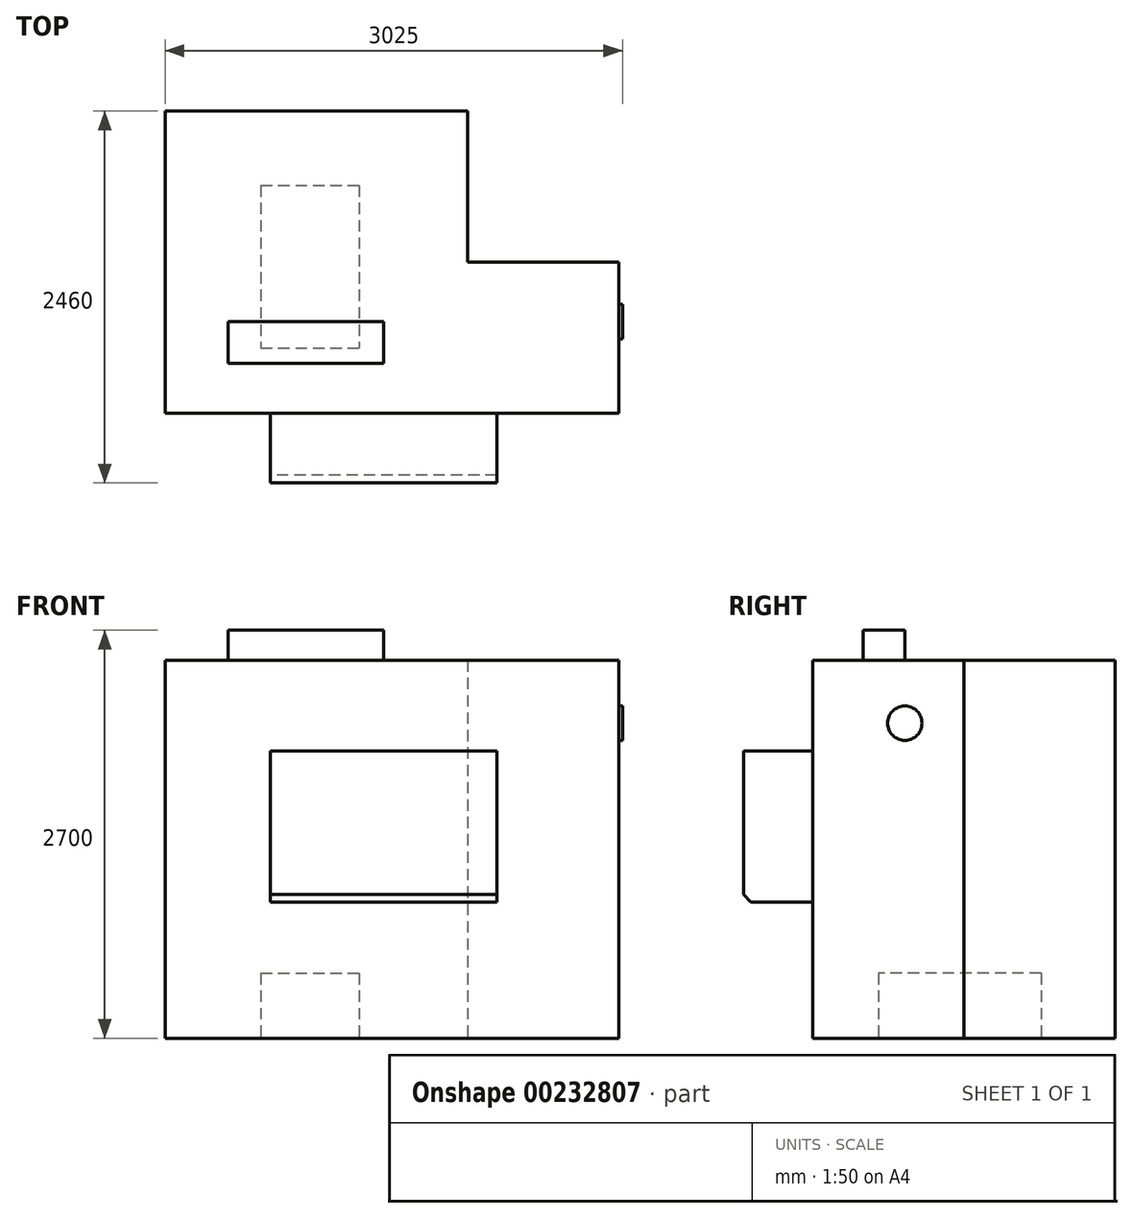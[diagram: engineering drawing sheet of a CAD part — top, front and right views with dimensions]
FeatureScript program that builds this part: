
annotation { "Feature Type Name" : "Feature", "Feature Type Description" : "" }
export const myFeature = defineFeature(function(context is Context, id is Id, definition is map)
    precondition{}
    {
        {
            var Q0;
            Q0=qCreatedBy(makeId("Top.planeOp"),FACE);
            var sketch = newSketch(context, id + "F0", { "sketchPlane" : qUnion([Q0])});
            skLineSegment(sketch, "E0", {"start": v(-1444.29, -607.78) * mm, "end": v(-1444.29, 1392.22) * mm});
            skLineSegment(sketch, "E1", {"start": v(-1444.29, 1392.22) * mm, "end": v(555.71, 1392.22) * mm});
            skLineSegment(sketch, "E2", {"start": v(555.71, 1392.22) * mm, "end": v(555.71, 392.22) * mm});
            skLineSegment(sketch, "E3", {"start": v(555.71, 392.22) * mm, "end": v(1555.71, 392.22) * mm});
            skLineSegment(sketch, "E4", {"start": v(1555.71, 392.22) * mm, "end": v(1555.71, -607.78) * mm});
            skLineSegment(sketch, "E5", {"start": v(1555.71, -607.78) * mm, "end": v(-1444.29, -607.78) * mm});
            skCircle(sketch, "E6", {"center": v(-627.12, 837.16) * mm, "radius": 250 * mm});
            skSolve(sketch);
        }
        {
            var Q0;
            Q0=makeQuery(id+"F0.imprint","IMPRINT",FACE,{"disambiguationData":[TD([[makeQuery(id+"F0.imprint","IMPRINT",EDGE,{"derivedFrom":sQuery(id+"F0.wireOp",EDGE,"E0")}),-1.0]])]});
            var Q1;
            Q1=makeQuery(id+"F0.imprint","IMPRINT",FACE,{"disambiguationData":[TD([[makeQuery(id+"F0.imprint","IMPRINT",EDGE,{"derivedFrom":sQuery(id+"F0.wireOp",EDGE,"E6")}),1.0]])]});
            extrude(context, id + "F1", {"entities" : qUnion([Q0, Q1]), "depth" : 2500 * mm});
        }
        {
            var Q0;
            Q0=makeQuery(id+"F1.opExtrude","CAP_FACE",FACE,{"disambiguationData":[OSD([sQuery(id+"F0.wireOp",EDGE,"E0"),sQuery(id+"F0.wireOp",EDGE,"E1"),sQuery(id+"F0.wireOp",EDGE,"E2"),sQuery(id+"F0.wireOp",EDGE,"E3"),sQuery(id+"F0.wireOp",EDGE,"E4"),sQuery(id+"F0.wireOp",EDGE,"E5")])],"isStart":true});
            var sketch = newSketch(context, id + "F2", { "sketchPlane" : qUnion([Q0])});
            skLineSegment(sketch, "E7.bottom", {"start": v(-811.32, -900.68) * mm, "end": v(-161.45, -900.68) * mm});
            skLineSegment(sketch, "E7.top", {"start": v(-811.32, 173.64) * mm, "end": v(-161.45, 173.64) * mm});
            skLineSegment(sketch, "E7.left", {"start": v(-811.32, -900.68) * mm, "end": v(-811.32, 173.64) * mm});
            skLineSegment(sketch, "E7.right", {"start": v(-161.45, -900.68) * mm, "end": v(-161.45, 173.64) * mm});
            skSolve(sketch);
        }
        {
            var Q0;
            Q0=makeQuery(id+"F2.imprint","IMPRINT",FACE,{"disambiguationData":[TD([[makeQuery(id+"F2.imprint","IMPRINT",EDGE,{"derivedFrom":sQuery(id+"F2.wireOp",EDGE,"E7.bottom")}),1.0]])]});
            extrude(context, id + "F3", {"entities" : qUnion([Q0]), "operationType" : NewBodyOperationType.REMOVE, "oppositeDirection" : true, "depth" : 430 * mm});
        }
        {
            var Q0;
            Q0=makeQuery(id+"F1.opExtrude","SWEPT_FACE",FACE,{"disambiguationData":[OSD([sQuery(id+"F0.wireOp",EDGE,"E5")])]});
            var sketch = newSketch(context, id + "F4", { "sketchPlane" : qUnion([Q0])});
            skLineSegment(sketch, "E8.bottom", {"start": v(750, 1900) * mm, "end": v(-750, 1900) * mm});
            skLineSegment(sketch, "E8.top", {"start": v(750, 900) * mm, "end": v(-750, 900) * mm});
            skLineSegment(sketch, "E8.left", {"start": v(750, 1900) * mm, "end": v(750, 900) * mm});
            skLineSegment(sketch, "E8.right", {"start": v(-750, 1900) * mm, "end": v(-750, 900) * mm});
            skPoint(sketch, "E8.middle", {"position": v(0, 1400) * mm});
            skSolve(sketch);
        }
        {
            var Q0;
            Q0=makeQuery(id+"F4.imprint","IMPRINT",FACE,{"disambiguationData":[TD([[makeQuery(id+"F4.imprint","IMPRINT",EDGE,{"derivedFrom":sQuery(id+"F4.wireOp",EDGE,"E8.bottom")}),1.0]])]});
            extrude(context, id + "F5", {"entities" : qUnion([Q0]), "operationType" : NewBodyOperationType.ADD, "depth" : 460 * mm});
        }
        {
            var Q0;
            Q0=makeQuery(id+"F1.opExtrude","SWEPT_FACE",FACE,{"disambiguationData":[OSD([sQuery(id+"F0.wireOp",EDGE,"E4")])]});
            var sketch = newSketch(context, id + "F6", { "sketchPlane" : qUnion([Q0])});
            skCircle(sketch, "E9", {"center": v(0, 2084.71) * mm, "radius": 113.61 * mm});
            skSolve(sketch);
        }
        {
            var Q0;
            Q0=makeQuery(id+"F6.imprint","IMPRINT",FACE,{"disambiguationData":[TD([[makeQuery(id+"F6.imprint","IMPRINT",EDGE,{"derivedFrom":sQuery(id+"F6.wireOp",EDGE,"E9")}),1.0]])]});
            extrude(context, id + "F7", {"entities" : qUnion([Q0]), "operationType" : NewBodyOperationType.ADD, "depth" : 25 * mm});
        }
        {
            var Q0;
            Q0=makeQuery(id+"F5.opExtrude","CAP_EDGE",EDGE,{"disambiguationData":[OSD([sQuery(id+"F4.wireOp",EDGE,"E8.top")])],"isStart":false});
            chamfer(context, id + "F8", {"entities" : qUnion([Q0]), "width" : 50 * mm, "tangentPropagation" : true});
        }
        {
            var Q0;
            Q0=makeQuery(id+"F1.opExtrude","CAP_FACE",FACE,{"disambiguationData":[OSD([sQuery(id+"F0.wireOp",EDGE,"E0"),sQuery(id+"F0.wireOp",EDGE,"E1"),sQuery(id+"F0.wireOp",EDGE,"E2"),sQuery(id+"F0.wireOp",EDGE,"E3"),sQuery(id+"F0.wireOp",EDGE,"E4"),sQuery(id+"F0.wireOp",EDGE,"E5")])],"isStart":false});
            var sketch = newSketch(context, id + "F9", { "sketchPlane" : qUnion([Q0])});
            skLineSegment(sketch, "E10.bottom", {"start": v(0, 0) * mm, "end": v(-1029.48, 0) * mm});
            skLineSegment(sketch, "E10.top", {"start": v(0, -276.77) * mm, "end": v(-1029.48, -276.77) * mm});
            skLineSegment(sketch, "E10.left", {"start": v(0, 0) * mm, "end": v(0, -276.77) * mm});
            skLineSegment(sketch, "E10.right", {"start": v(-1029.48, 0) * mm, "end": v(-1029.48, -276.77) * mm});
            skPoint(sketch, "E10.middle", {"position": v(-514.74, -138.38) * mm});
            skSolve(sketch);
        }
        {
            var Q0;
            Q0=makeQuery(id+"F9.imprint","IMPRINT",FACE,{"disambiguationData":[TD([[makeQuery(id+"F9.imprint","IMPRINT",EDGE,{"derivedFrom":sQuery(id+"F9.wireOp",EDGE,"E10.bottom")}),1.0]])]});
            extrude(context, id + "F10", {"entities" : qUnion([Q0]), "depth" : 200 * mm});
        }
    });
